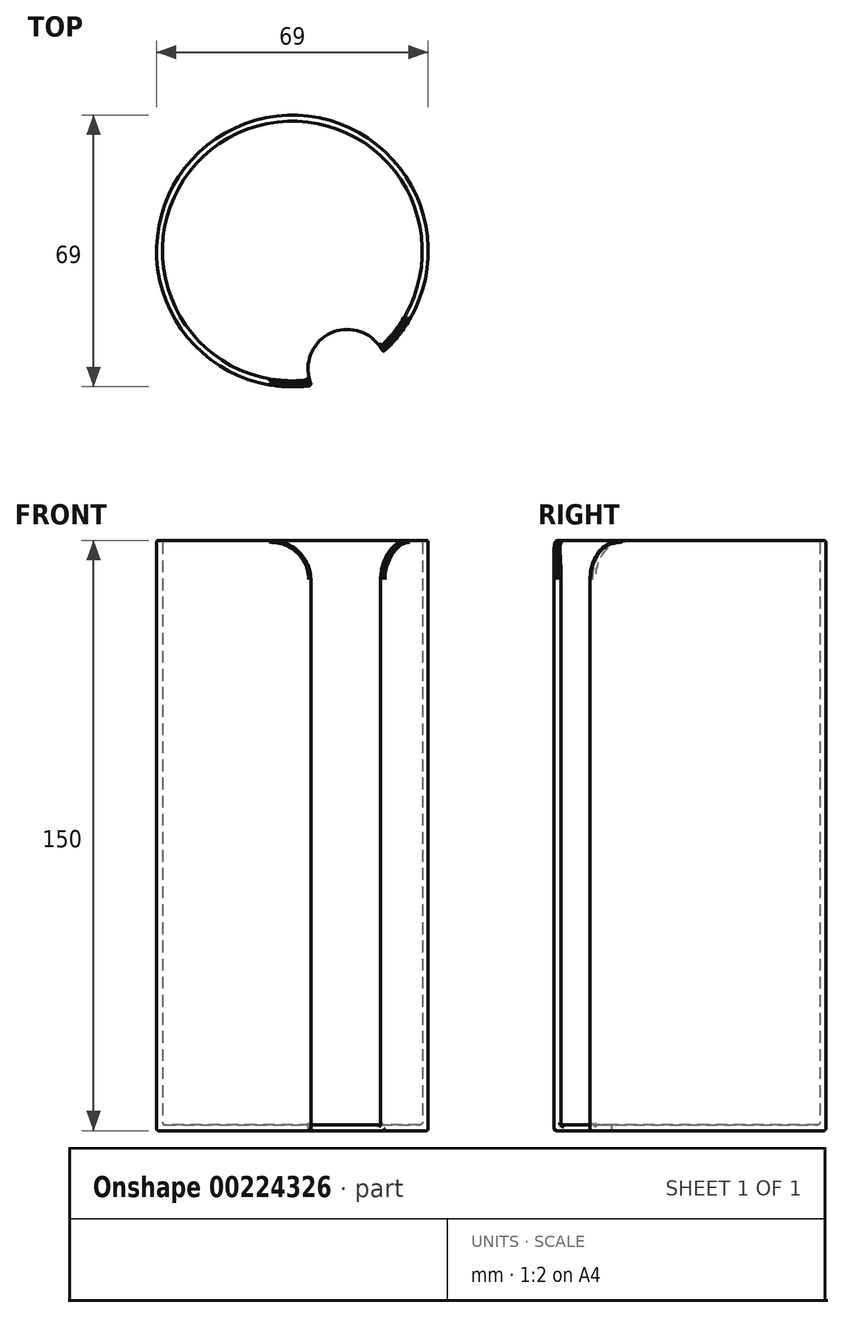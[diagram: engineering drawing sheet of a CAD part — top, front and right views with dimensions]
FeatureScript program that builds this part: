
annotation { "Feature Type Name" : "Feature", "Feature Type Description" : "" }
export const myFeature = defineFeature(function(context is Context, id is Id, definition is map)
    precondition{}
    {
        {
            var Q0;
            Q0=qCreatedBy(makeId("Top.planeOp"),FACE);
            var sketch = newSketch(context, id + "F0", { "sketchPlane" : qUnion([Q0])});
            skCircle(sketch, "E0", {"center": v(-54, 30.6) * mm, "radius": 34.5 * mm});
            skArc(sketch, "E1", {"start": v(-30.97, 4.9) * mm, "mid": v(-44.26, 9.74) * mm, "end": v(-49.1, -3.55) * mm});
            skCircle(sketch, "E2", {"center": v(-54, 30.6) * mm, "radius": 42.5 * mm});
            skSolve(sketch);
        }
        {
            var Q0;
            {var subQ0=sQuery(id+"F0.wireOp",EDGE,"E1");Q0=makeQuery(id+"F0.imprint","IMPRINT",FACE,{"disambiguationData":[TD([[makeQuery(id+"F0.imprint","IMPRINT",EDGE,{"derivedFrom":subQ0}),-1.0]])]});}
            extrude(context, id + "F1", {"entities" : qUnion([Q0]), "depth" : 150 * mm});
        }
        {
            var Q0;
            Q0=makeQuery(id+"F1.opExtrude","CAP_FACE",FACE,{"disambiguationData":[OSD([sQuery(id+"F0.wireOp",EDGE,"E0"),sQuery(id+"F0.wireOp",EDGE,"E1")])],"isStart":false});
            var Q1;
            Q1=makeQuery(id+"F1.opExtrude","SWEPT_FACE",FACE,{"disambiguationData":[OSD([sQuery(id+"F0.wireOp",EDGE,"E1")])]});
            shell(context, id + "F2", {"entities" : qUnion([Q0, Q1]), "thickness" : 1.5 * mm});
        }
        {
            var Q0;
            Q0=makeQuery(id+"F1.opExtrude","CAP_EDGE",EDGE,{"disambiguationData":[OSD([sQuery(id+"F0.wireOp",EDGE,"E0")])],"isStart":false});
            var Q1;
            {var subQ0=sQuery(id+"F0.wireOp",EDGE,"E0");Q1=makeQuery(id+"F2.opShell","OFFSET_EDGE",EDGE,{"disambiguationData":[OSD([subQ0]),TDD([makeQuery(id+"F1.opExtrude","CAP_EDGE",EDGE,{"disambiguationData":[OSD([subQ0])],"isStart":false})])]});}
            var Q2;
            {var subQ0=sQuery(id+"F0.wireOp",EDGE,"E1");var subQ1=sQuery(id+"F0.wireOp",EDGE,"E0");Q2=makeQuery(id+"F2.opShell","OFFSET_EDGE",EDGE,{"disambiguationData":[OSD([subQ1,subQ0]),TDD([makeQuery(id+"F1.opExtrude","SWEPT_EDGE",EDGE,{"disambiguationData":[OSD([subQ1,subQ0]),TDD([makeQuery(id+"F0.imprint","INTERSECT",VERTEX,{"disambiguationData":[OD(0.0)],"derivedFrom":[subQ1,subQ0]})])]})])]});}
            var Q3;
            {var subQ0=sQuery(id+"F0.wireOp",EDGE,"E1");var subQ1=sQuery(id+"F0.wireOp",EDGE,"E0");Q3=makeQuery(id+"F1.opExtrude","SWEPT_EDGE",EDGE,{"disambiguationData":[OSD([subQ1,subQ0]),TDD([makeQuery(id+"F0.imprint","INTERSECT",VERTEX,{"disambiguationData":[OD(0.0)],"derivedFrom":[subQ1,subQ0]})])]});}
            var Q4;
            {var subQ0=sQuery(id+"F0.wireOp",EDGE,"E1");var subQ1=sQuery(id+"F0.wireOp",EDGE,"E0");Q4=makeQuery(id+"F1.opExtrude","SWEPT_EDGE",EDGE,{"disambiguationData":[OSD([subQ1,subQ0]),TDD([makeQuery(id+"F0.imprint","INTERSECT",VERTEX,{"disambiguationData":[OD(1.0)],"derivedFrom":[subQ1,subQ0]})])]});}
            var Q5;
            {var subQ0=sQuery(id+"F0.wireOp",EDGE,"E1");var subQ1=sQuery(id+"F0.wireOp",EDGE,"E0");Q5=makeQuery(id+"F2.opShell","OFFSET_EDGE",EDGE,{"disambiguationData":[OSD([subQ1,subQ0]),TDD([makeQuery(id+"F1.opExtrude","SWEPT_EDGE",EDGE,{"disambiguationData":[OSD([subQ1,subQ0]),TDD([makeQuery(id+"F0.imprint","INTERSECT",VERTEX,{"disambiguationData":[OD(1.0)],"derivedFrom":[subQ1,subQ0]})])]})])]});}
            var Q6;
            {var subQ0=sQuery(id+"F0.wireOp",EDGE,"E1");Q6=makeQuery(id+"F2.opShell","OFFSET_EDGE",EDGE,{"disambiguationData":[OSD([subQ0]),TDD([makeQuery(id+"F1.opExtrude","CAP_EDGE",EDGE,{"disambiguationData":[OSD([subQ0])],"isStart":true})])]});}
            var Q7;
            Q7=makeQuery(id+"F1.opExtrude","CAP_EDGE",EDGE,{"disambiguationData":[OSD([sQuery(id+"F0.wireOp",EDGE,"E0")])],"isStart":true});
            var Q8;
            {var subQ0=sQuery(id+"F0.wireOp",EDGE,"E0");Q8=makeQuery(id+"F2.opShell","OFFSET_EDGE",EDGE,{"disambiguationData":[OSD([subQ0]),TDD([makeQuery(id+"F1.opExtrude","CAP_EDGE",EDGE,{"disambiguationData":[OSD([subQ0])],"isStart":true})])]});}
            fillet(context, id + "F3", {"entities" : qUnion([Q0, Q1, Q2, Q3, Q4, Q5, Q6, Q7, Q8]), "radius" : 0.5 * mm, "tangentPropagation" : true, "allowEdgeOverflow" : false});
        }
        {
            var Q0;
            Q0=makeQuery(id+"F1.opExtrude","CAP_EDGE",EDGE,{"disambiguationData":[OSD([sQuery(id+"F0.wireOp",EDGE,"E1")])],"isStart":false});
            var Q1;
            {var subQ0=sQuery(id+"F0.wireOp",EDGE,"E1");Q1=makeQuery(id+"F2.opShell","OFFSET_EDGE",EDGE,{"disambiguationData":[OSD([subQ0]),TDD([makeQuery(id+"F1.opExtrude","CAP_EDGE",EDGE,{"disambiguationData":[OSD([subQ0])],"isStart":false})])]});}
            fillet(context, id + "F4", {"entities" : qUnion([Q0, Q1]), "radius" : 10 * mm, "tangentPropagation" : true, "allowEdgeOverflow" : false});
        }
    });
